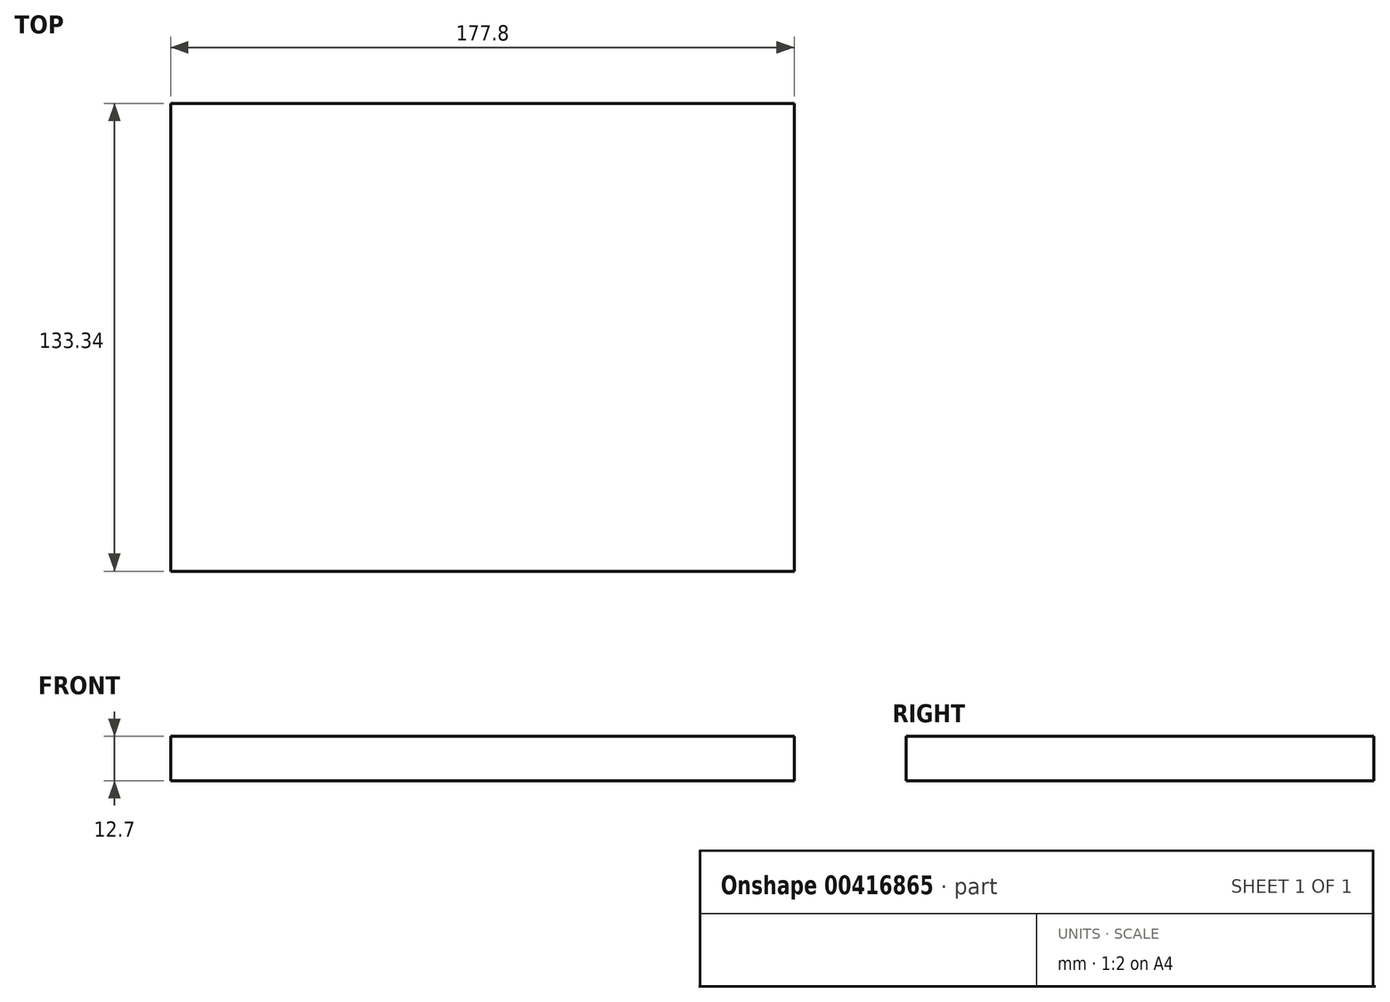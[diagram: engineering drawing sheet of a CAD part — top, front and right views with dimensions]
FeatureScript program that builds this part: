
annotation { "Feature Type Name" : "Feature", "Feature Type Description" : "" }
export const myFeature = defineFeature(function(context is Context, id is Id, definition is map)
    precondition{}
    {
        {
            var Q0;
            Q0=qCreatedBy(makeId("Top.planeOp"),FACE);
            var sketch = newSketch(context, id + "F0", { "sketchPlane" : qUnion([Q0])});
            skLineSegment(sketch, "E0.bottom", {"start": v(-88.9, 66.68) * mm, "end": v(88.9, 66.68) * mm});
            skLineSegment(sketch, "E0.top", {"start": v(-88.9, -66.68) * mm, "end": v(88.9, -66.68) * mm});
            skLineSegment(sketch, "E0.left", {"start": v(-88.9, 66.68) * mm, "end": v(-88.9, -66.68) * mm});
            skLineSegment(sketch, "E0.right", {"start": v(88.9, 66.68) * mm, "end": v(88.9, -66.68) * mm});
            skPoint(sketch, "E0.middle", {"position": v(0, 0) * mm});
            skSolve(sketch);
        }
        {
            var Q0;
            Q0 = qSketchRegion(id + "F0", true);
            extrude(context, id + "F1", {"entities" : qUnion([Q0]), "depth" : 12.7 * mm});
        }
    });
